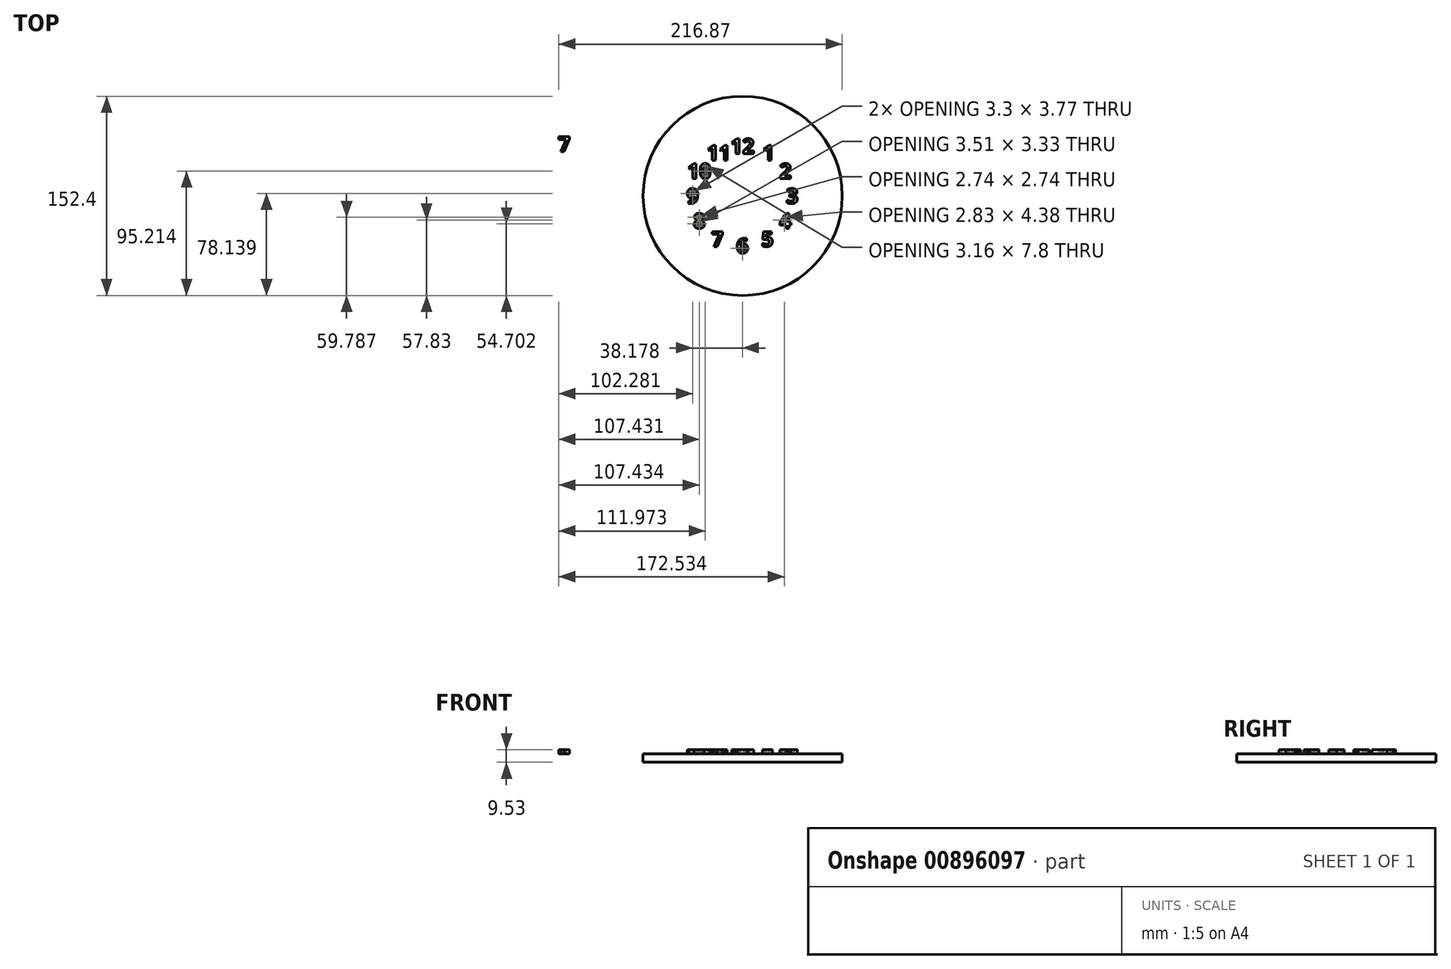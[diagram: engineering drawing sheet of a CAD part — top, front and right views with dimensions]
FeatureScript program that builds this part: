
annotation { "Feature Type Name" : "Feature", "Feature Type Description" : "" }
export const myFeature = defineFeature(function(context is Context, id is Id, definition is map)
    precondition{}
    {
        {
            var Q0;
            Q0=qCreatedBy(makeId("Top.planeOp"),FACE);
            var sketch = newSketch(context, id + "F0", { "sketchPlane" : qUnion([Q0])});
            skCircle(sketch, "E0", {"center": v(0, 0) * mm, "radius": 76.2 * mm});
            skPoint(sketch, "E1", {"position": v(0, 58.42) * mm});
            skPoint(sketch, "E2.1.0", {"position": v(-29.2, 50.6) * mm});
            skPoint(sketch, "E2.2.0", {"position": v(-50.6, 29.21) * mm});
            skPoint(sketch, "E3.0.3.0", {"position": v(-58.42, 0) * mm});
            skPoint(sketch, "E3.0.4.0", {"position": v(-50.6, -29.2) * mm});
            skPoint(sketch, "E3.0.5.0", {"position": v(-29.2, -50.6) * mm});
            skPoint(sketch, "E3.0.6.0", {"position": v(0, -58.42) * mm});
            skPoint(sketch, "E3.0.7.0", {"position": v(29.2, -50.6) * mm});
            skPoint(sketch, "E3.0.8.0", {"position": v(50.6, -29.21) * mm});
            skPoint(sketch, "E3.0.9.0", {"position": v(58.42, 0) * mm});
            skPoint(sketch, "E3.0.10.0", {"position": v(50.6, 29.21) * mm});
            skPoint(sketch, "E3.0.11.0", {"position": v(29.21, 50.6) * mm});
            skSolve(sketch);
        }
        {
            var Q0;
            Q0=makeQuery(id+"F0.imprint","IMPRINT",FACE,{"disambiguationData":[TD([[makeQuery(id+"F0.imprint","IMPRINT",EDGE,{"derivedFrom":sQuery(id+"F0.wireOp",EDGE,"E0")}),1.0]])]});
            extrude(context, id + "F1", {"entities" : qUnion([Q0]), "oppositeDirection" : true, "depth" : 6.35 * mm, "offsetDistance" : 25.4 * mm});
        }
        {
            var Q0;
            Q0=qCreatedBy(makeId("Top.planeOp"),FACE);
            var sketch = newSketch(context, id + "F2", { "sketchPlane" : qUnion([Q0])});
            skText(sketch, "E4", { "text": "1", "fontName": "OpenSans-Bold.ttf"});
            skText(sketch, "E5", { "text": "2", "fontName": "OpenSans-Bold.ttf"});
            skText(sketch, "E6", { "text": "3", "fontName": "OpenSans-Bold.ttf"});
            skText(sketch, "E7", { "text": "4", "fontName": "OpenSans-Bold.ttf"});
            skText(sketch, "E8", { "text": "5", "fontName": "OpenSans-Bold.ttf"});
            skText(sketch, "E9", { "text": "6", "fontName": "OpenSans-Bold.ttf"});
            skText(sketch, "E10", { "text": "7", "fontName": "OpenSans-Bold.ttf"});
            skPoint(sketch, "E11", {"position": v(0, 38.1) * mm});
            skPoint(sketch, "E12.1.0", {"position": v(-19.05, 33) * mm});
            skPoint(sketch, "E12.2.0", {"position": v(-33, 19.05) * mm});
            skPoint(sketch, "E12.3.0", {"position": v(-38.1, 0) * mm});
            skPoint(sketch, "E12.4.0", {"position": v(-33, -19.05) * mm});
            skPoint(sketch, "E12.5.0", {"position": v(-19.05, -33) * mm});
            skPoint(sketch, "E12.6.0", {"position": v(0, -38.1) * mm});
            skPoint(sketch, "E12.7.0", {"position": v(19.05, -33) * mm});
            skPoint(sketch, "E12.8.0", {"position": v(33, -19.05) * mm});
            skPoint(sketch, "E12.9.0", {"position": v(38.1, 0) * mm});
            skPoint(sketch, "E12.10.0", {"position": v(33, 19.05) * mm});
            skPoint(sketch, "E12.11.0", {"position": v(19.05, 33) * mm});
            skPoint(sketch, "E12.center", {"position": v(0, 0) * mm});
            skLineSegment(sketch, "E13", {"start": v(15.26, 33) * mm, "end": v(22.84, 33) * mm, "construction": true});
            skLineSegment(sketch, "E14", {"start": v(28.07, -19.05) * mm, "end": v(37.92, -19.05) * mm, "construction": true});
            skText(sketch, "E15", { "text": "8", "fontName": "OpenSans-Bold.ttf"});
            skText(sketch, "E16", { "text": "9", "fontName": "OpenSans-Bold.ttf"});
            skText(sketch, "E17", { "text": "10", "fontName": "OpenSans-Bold.ttf"});
            skText(sketch, "E18", { "text": "11", "fontName": "OpenSans-Bold.ttf"});
            skText(sketch, "E19", { "text": "12", "fontName": "OpenSans-Bold.ttf"});
            skText(sketch, "E20", { "text": "7", "fontName": "OpenSans-Bold.ttf"});
            const initialGuessF2  = {"E4": [0.01526, 0.02728, 1, 0, 0.01143], "E5": [0.0282, 0.01334, 1, 0, 0.01143], "E6": [0.03336, -0.00572, 1, 0, 0.01143], "E7": [0.02807, -0.02477, 1, 0, 0.01143], "E8": [0.01436, -0.03871, 1, 0, 0.01143], "E9": [-0.0048, -0.04382, 1, 0, 0.01143], "E10": [-0.02384, -0.03871, 1, 0, 0.01143], "E15": [-0.03777, -0.02477, 1, 0, 0.01143], "E16": [-0.04287, -0.00572, 1, 0, 0.01143], "E17": [-0.04229, 0.01334, 1, 0, 0.01143], "E18": [-0.02737, 0.02728, 1, 0, 0.01143], "E19": [-0.00932, 0.03239, 1, 0, 0.01143], "E20": [-0.1411, 0.0339, 1, 0, 0.01143]};
            skSetInitialGuess(sketch, initialGuessF2);
            skSolve(sketch);
        }
        {
            var Q0;
            Q0 = qSketchRegion(id + "F2", true);
            extrude(context, id + "F3", {"entities" : qUnion([Q0]), "depth" : 3.17 * mm, "offsetDistance" : 25.4 * mm});
        }
    });
